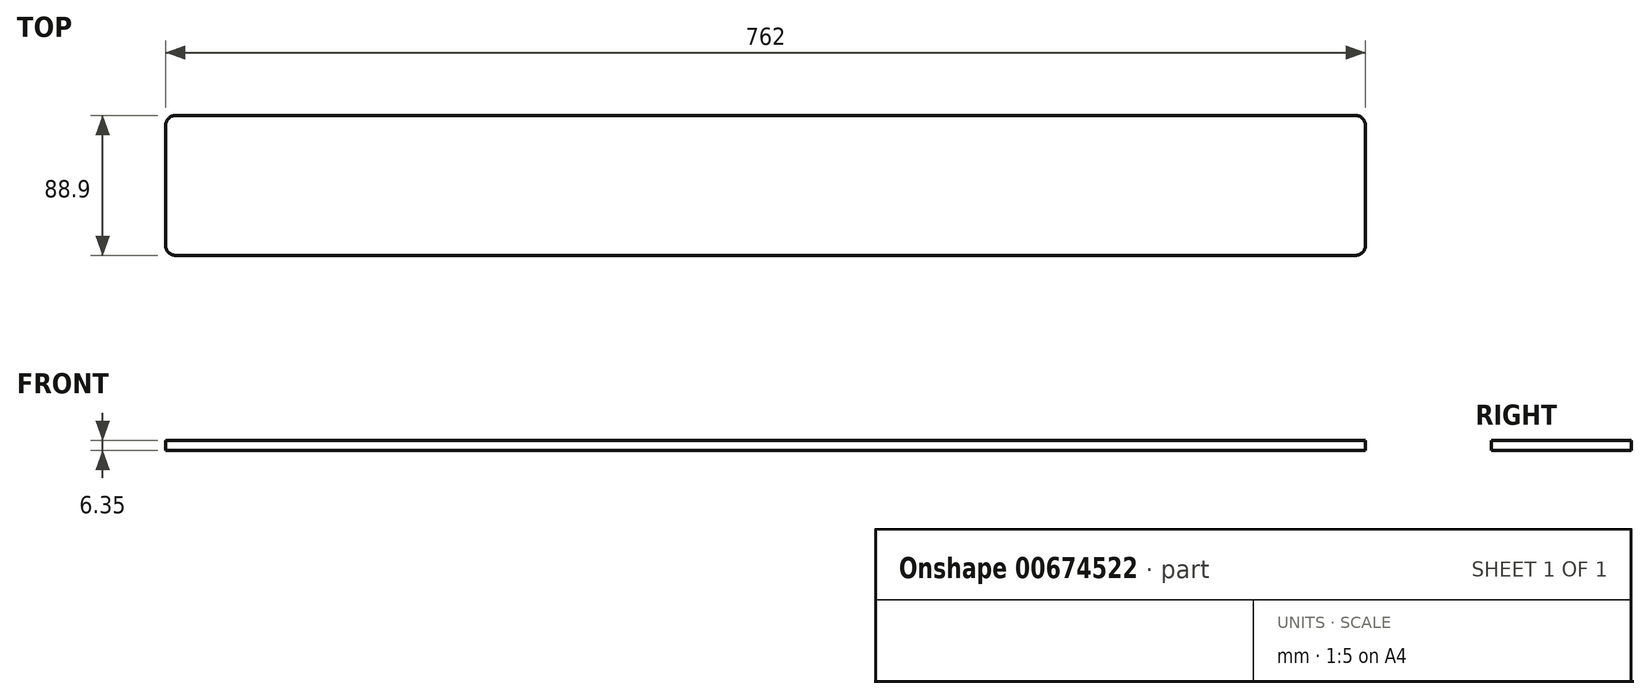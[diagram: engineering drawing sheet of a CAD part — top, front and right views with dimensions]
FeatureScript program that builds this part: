
annotation { "Feature Type Name" : "Feature", "Feature Type Description" : "" }
export const myFeature = defineFeature(function(context is Context, id is Id, definition is map)
    precondition{}
    {
        {
            var Q0;
            Q0=qCreatedBy(makeId("Top.planeOp"),FACE);
            var sketch = newSketch(context, id + "F0", { "sketchPlane" : qUnion([Q0])});
            skLineSegment(sketch, "E0.bottom", {"start": v(374.65, 44.45) * mm, "end": v(-374.65, 44.45) * mm});
            skLineSegment(sketch, "E0.top", {"start": v(374.65, -44.45) * mm, "end": v(-374.65, -44.45) * mm});
            skLineSegment(sketch, "E0.left", {"start": v(381, 38.1) * mm, "end": v(381, -38.1) * mm});
            skLineSegment(sketch, "E0.right", {"start": v(-381, 38.1) * mm, "end": v(-381, -38.1) * mm});
            skPoint(sketch, "E0.middle", {"position": v(0, 0) * mm});
            skPoint(sketch, "E1.visualSharp", {"position": v(381, 44.45) * mm});
            skArc(sketch, "E1.filletArc", {"start": v(381, 38.1) * mm, "mid": v(379.14, 42.6) * mm, "end": v(374.65, 44.45) * mm});
            skPoint(sketch, "E2.visualSharp", {"position": v(381, -44.45) * mm});
            skArc(sketch, "E2.filletArc", {"start": v(374.65, -44.45) * mm, "mid": v(379.14, -42.6) * mm, "end": v(381, -38.1) * mm});
            skPoint(sketch, "E3.visualSharp", {"position": v(-381, -44.45) * mm});
            skArc(sketch, "E3.filletArc", {"start": v(-381, -38.1) * mm, "mid": v(-379.14, -42.6) * mm, "end": v(-374.65, -44.45) * mm});
            skPoint(sketch, "E4.visualSharp", {"position": v(-381, 44.45) * mm});
            skArc(sketch, "E4.filletArc", {"start": v(-374.65, 44.45) * mm, "mid": v(-379.14, 42.6) * mm, "end": v(-381, 38.1) * mm});
            skSolve(sketch);
        }
        {
            var Q0;
            Q0 = qSketchRegion(id + "F0", true);
            extrude(context, id + "F1", {"entities" : qUnion([Q0]), "depth" : 6.35 * mm, "offsetDistance" : 25.4 * mm});
        }
    });
